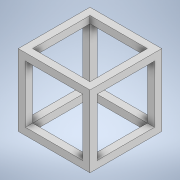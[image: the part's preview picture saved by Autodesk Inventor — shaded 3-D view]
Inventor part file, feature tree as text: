
AUTODESK INVENTOR PART (.ipt)
format: ipt  version: 2022 (Build 260153000, 153)  size: 141,824 bytes
history: native  units: in
note: dims shown in document units (in); Inventor stores cm internally (conversion verified against a paired STEP export)
features: extrude x4, sketch x4
ambient origin geometry x8: Origin, YZ Plane, XZ Plane, XY Plane, X Axis, Y Axis, Z Axis, Center Point
bodies: Solid1 (feature_tree)
feature tree (8):
  extrude  "Extrusion1"  Depth=2.5in
  extrude  "Extrusion2"  Depth=2.0in
  extrude  "Extrusion3"  TaperAngle=0.0deg  [1 undecoded]
  extrude  "Extrusion4"  Depth=2.0in
  sketch  "Sketch1"  dims[d0=2.5in d1=2.5in]
  sketch  "Sketch2"  dims[d2=2.5in d3=0.0in d4=2.0in]
  sketch  "Sketch3"  dims[d5=2.0in d6=0.0in d7=0.0in]
  sketch  "Sketch4"  dims[d8=2.0in d9=2.0in d10=0.0in d11=0.0in d12=2.0in d13=2.0in d14=0.0in d15=0.0in]
note: 1 required parameter value undecoded (feature->parameter linkage not recoverable at this tier; creation-order binding heuristic only, values carry confidence <= 0.55)
